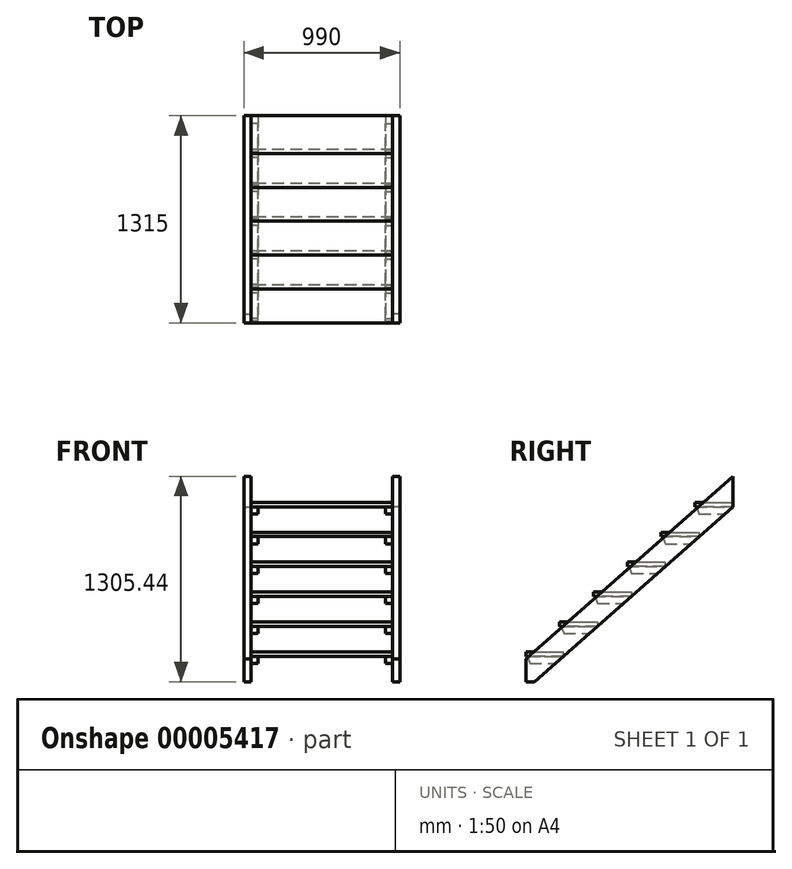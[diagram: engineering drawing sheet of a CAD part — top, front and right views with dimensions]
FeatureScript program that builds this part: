
annotation { "Feature Type Name" : "Feature", "Feature Type Description" : "" }
export const myFeature = defineFeature(function(context is Context, id is Id, definition is map)
    precondition{}
    {
        {
            var Q0;
            Q0=qCreatedBy(makeId("Right.planeOp"),FACE);
            var sketch = newSketch(context, id + "F0", { "sketchPlane" : qUnion([Q0])});
            skLineSegment(sketch, "E0.bottom", {"start": v(0, 0) * mm, "end": v(240, 0) * mm});
            skLineSegment(sketch, "E0.top", {"start": v(0, 28) * mm, "end": v(240, 28) * mm});
            skLineSegment(sketch, "E0.left", {"start": v(0, 0) * mm, "end": v(0, 28) * mm});
            skLineSegment(sketch, "E0.right", {"start": v(240, 0) * mm, "end": v(240, 28) * mm});
            skLineSegment(sketch, "E1.bottom", {"start": v(215, 218) * mm, "end": v(455, 218) * mm});
            skLineSegment(sketch, "E1.top", {"start": v(215, 190) * mm, "end": v(455, 190) * mm});
            skLineSegment(sketch, "E1.left", {"start": v(215, 218) * mm, "end": v(215, 190) * mm});
            skLineSegment(sketch, "E1.right", {"start": v(455, 218) * mm, "end": v(455, 190) * mm});
            skLineSegment(sketch, "E2.bottom", {"start": v(430, 408) * mm, "end": v(670, 408) * mm});
            skLineSegment(sketch, "E2.top", {"start": v(430, 380) * mm, "end": v(670, 380) * mm});
            skLineSegment(sketch, "E2.left", {"start": v(430, 408) * mm, "end": v(430, 380) * mm});
            skLineSegment(sketch, "E2.right", {"start": v(670, 408) * mm, "end": v(670, 380) * mm});
            skLineSegment(sketch, "E3.bottom", {"start": v(645, 598) * mm, "end": v(885, 598) * mm});
            skLineSegment(sketch, "E3.top", {"start": v(645, 570) * mm, "end": v(885, 570) * mm});
            skLineSegment(sketch, "E3.left", {"start": v(645, 598) * mm, "end": v(645, 570) * mm});
            skLineSegment(sketch, "E3.right", {"start": v(885, 598) * mm, "end": v(885, 570) * mm});
            skLineSegment(sketch, "E4.bottom", {"start": v(860, 788) * mm, "end": v(1100, 788) * mm});
            skLineSegment(sketch, "E4.top", {"start": v(860, 760) * mm, "end": v(1100, 760) * mm});
            skLineSegment(sketch, "E4.left", {"start": v(860, 788) * mm, "end": v(860, 760) * mm});
            skLineSegment(sketch, "E4.right", {"start": v(1100, 788) * mm, "end": v(1100, 760) * mm});
            skLineSegment(sketch, "E5.bottom", {"start": v(1075, 978) * mm, "end": v(1315, 978) * mm});
            skLineSegment(sketch, "E5.top", {"start": v(1075, 950) * mm, "end": v(1315, 950) * mm});
            skLineSegment(sketch, "E5.left", {"start": v(1075, 978) * mm, "end": v(1075, 950) * mm});
            skLineSegment(sketch, "E5.right", {"start": v(1315, 978) * mm, "end": v(1315, 950) * mm});
            skSolve(sketch);
        }
        {
            var Q0;
            Q0=makeQuery(id+"F0.imprint","IMPRINT",FACE,{"disambiguationData":[TD([[makeQuery(id+"F0.imprint","IMPRINT",EDGE,{"derivedFrom":sQuery(id+"F0.wireOp",EDGE,"E0.bottom")}),1.0]])]});
            var Q1;
            Q1=makeQuery(id+"F0.imprint","IMPRINT",FACE,{"disambiguationData":[TD([[makeQuery(id+"F0.imprint","IMPRINT",EDGE,{"derivedFrom":sQuery(id+"F0.wireOp",EDGE,"E1.bottom")}),-1.0]])]});
            var Q2;
            Q2=makeQuery(id+"F0.imprint","IMPRINT",FACE,{"disambiguationData":[TD([[makeQuery(id+"F0.imprint","IMPRINT",EDGE,{"derivedFrom":sQuery(id+"F0.wireOp",EDGE,"E4.bottom")}),-1.0]])]});
            var Q3;
            Q3=makeQuery(id+"F0.imprint","IMPRINT",FACE,{"disambiguationData":[TD([[makeQuery(id+"F0.imprint","IMPRINT",EDGE,{"derivedFrom":sQuery(id+"F0.wireOp",EDGE,"E3.bottom")}),-1.0]])]});
            var Q4;
            Q4=makeQuery(id+"F0.imprint","IMPRINT",FACE,{"disambiguationData":[TD([[makeQuery(id+"F0.imprint","IMPRINT",EDGE,{"derivedFrom":sQuery(id+"F0.wireOp",EDGE,"E5.bottom")}),-1.0]])]});
            var Q5;
            Q5=makeQuery(id+"F0.imprint","IMPRINT",FACE,{"disambiguationData":[TD([[makeQuery(id+"F0.imprint","IMPRINT",EDGE,{"derivedFrom":sQuery(id+"F0.wireOp",EDGE,"E2.bottom")}),-1.0]])]});
            var Q6;
            Q6=makeQuery(id+"F0.imprint","IMPRINT",FACE,{"disambiguationData":[TD([[makeQuery(id+"F0.imprint","IMPRINT",EDGE,{"derivedFrom":sQuery(id+"F0.wireOp",EDGE,"670252bf-9cfb-4d57-b23d-327e6f0d2165.bottom")}),-1.0]])]});
            var Q7;
            Q7=makeQuery(id+"F0.imprint","IMPRINT",FACE,{"disambiguationData":[TD([[makeQuery(id+"F0.imprint","IMPRINT",EDGE,{"derivedFrom":sQuery(id+"F0.wireOp",EDGE,"97e81333-a598-4cda-a3b6-67043b5d0b65.bottom")}),-1.0]])]});
            extrude(context, id + "F1", {"entities" : qUnion([Q0, Q1, Q2, Q3, Q4, Q5, Q6, Q7]), "depth" : 900 * mm});
        }
        {
            var Q0;
            Q0=makeQuery(id+"F1.opExtrude","CAP_FACE",FACE,{"disambiguationData":[OSD([sQuery(id+"F0.wireOp",EDGE,"E0.bottom"),sQuery(id+"F0.wireOp",EDGE,"E0.top"),sQuery(id+"F0.wireOp",EDGE,"E0.left"),sQuery(id+"F0.wireOp",EDGE,"E0.right")])],"isStart":false});
            var sketch = newSketch(context, id + "F2", { "sketchPlane" : qUnion([Q0])});
            skLineSegment(sketch, "E6", {"start": v(55.73, -162) * mm, "end": v(0, -162) * mm});
            skLineSegment(sketch, "E7", {"start": v(0, -17.77) * mm, "end": v(1127.65, 978) * mm});
            skLineSegment(sketch, "E8", {"start": v(1127.65, 978) * mm, "end": v(1315, 978) * mm});
            skLineSegment(sketch, "E9", {"start": v(1315, 978) * mm, "end": v(1315, 950) * mm});
            skLineSegment(sketch, "E10", {"start": v(1315, 950) * mm, "end": v(55.73, -162) * mm});
            skLineSegment(sketch, "E11", {"start": v(1315, 978) * mm, "end": v(1315, 1143.44) * mm});
            skLineSegment(sketch, "E12", {"start": v(1127.65, 978) * mm, "end": v(1315, 1143.44) * mm});
            skLineSegment(sketch, "E13", {"start": v(0, -17.77) * mm, "end": v(0, -162) * mm});
            skSolve(sketch);
        }
        {
            var Q0;
            Q0 = qSketchRegion(id + "F2", true);
            extrude(context, id + "F3", {"entities" : qUnion([Q0]), "depth" : 45 * mm});
        }
        {
            var Q0;
            Q0=makeQuery(id+"F3.opExtrude","CAP_FACE",FACE,{"disambiguationData":[OSD([sQuery(id+"F2.wireOp",EDGE,"E6"),sQuery(id+"F2.wireOp",EDGE,"708b9f7f-88d3-4525-9253-f1f07b30f08b"),sQuery(id+"F2.wireOp",EDGE,"E7"),sQuery(id+"F2.wireOp",EDGE,"E8"),sQuery(id+"F2.wireOp",EDGE,"E9"),sQuery(id+"F2.wireOp",EDGE,"E10")])],"isStart":true});
            var sketch = newSketch(context, id + "F4", { "sketchPlane" : qUnion([Q0])});
            skLineSegment(sketch, "E14", {"start": v(-1315, 950) * mm, "end": v(-1085, 950) * mm});
            skLineSegment(sketch, "E15", {"start": v(-1085, 950) * mm, "end": v(-1101.38, 905) * mm});
            skLineSegment(sketch, "E16", {"start": v(-1101.38, 905) * mm, "end": v(-1264.04, 905) * mm});
            skLineSegment(sketch, "E17", {"start": v(-1264.04, 905) * mm, "end": v(-1315, 950) * mm});
            skLineSegment(sketch, "E18", {"start": v(-1099.84, 760) * mm, "end": v(-870, 760) * mm});
            skLineSegment(sketch, "E19", {"start": v(-870, 760) * mm, "end": v(-886.38, 715) * mm});
            skLineSegment(sketch, "E20", {"start": v(-886.38, 715) * mm, "end": v(-1048.88, 715) * mm});
            skLineSegment(sketch, "E21", {"start": v(-1048.88, 715) * mm, "end": v(-1099.84, 760) * mm});
            skLineSegment(sketch, "E22", {"start": v(-884.68, 570) * mm, "end": v(-655, 570) * mm});
            skLineSegment(sketch, "E23", {"start": v(-655, 570) * mm, "end": v(-671.38, 525) * mm});
            skLineSegment(sketch, "E24", {"start": v(-671.38, 525) * mm, "end": v(-833.72, 525) * mm});
            skLineSegment(sketch, "E25", {"start": v(-833.72, 525) * mm, "end": v(-884.68, 570) * mm});
            skLineSegment(sketch, "E26", {"start": v(-669.51, 380) * mm, "end": v(-440, 380) * mm});
            skLineSegment(sketch, "E27", {"start": v(-440, 380) * mm, "end": v(-456.38, 335) * mm});
            skLineSegment(sketch, "E28", {"start": v(-456.38, 335) * mm, "end": v(-618.55, 335) * mm});
            skLineSegment(sketch, "E29", {"start": v(-618.55, 335) * mm, "end": v(-669.51, 380) * mm});
            skLineSegment(sketch, "E30", {"start": v(-454.35, 190) * mm, "end": v(-225, 190) * mm});
            skLineSegment(sketch, "E31", {"start": v(-225, 190) * mm, "end": v(-241.38, 145) * mm});
            skLineSegment(sketch, "E32", {"start": v(-241.38, 145) * mm, "end": v(-403.4, 145) * mm});
            skLineSegment(sketch, "E33", {"start": v(-403.4, 145) * mm, "end": v(-454.35, 190) * mm});
            skLineSegment(sketch, "E34", {"start": v(-239.19, 0) * mm, "end": v(-10, 0) * mm});
            skLineSegment(sketch, "E35", {"start": v(-10, 0) * mm, "end": v(-26.38, -45) * mm});
            skLineSegment(sketch, "E36", {"start": v(-26.38, -45) * mm, "end": v(-188.23, -45) * mm});
            skLineSegment(sketch, "E37", {"start": v(-188.23, -45) * mm, "end": v(-239.19, 0) * mm});
            skSolve(sketch);
        }
        {
            var Q0;
            Q0 = qSketchRegion(id + "F4", true);
            extrude(context, id + "F5", {"entities" : qUnion([Q0]), "depth" : 45 * mm});
        }
        {
            var Q0;
            Q0=makeQuery(id+"F3.opExtrude","CAP_FACE",FACE,{"disambiguationData":[OSD([sQuery(id+"F2.wireOp",EDGE,"E6"),sQuery(id+"F2.wireOp",EDGE,"708b9f7f-88d3-4525-9253-f1f07b30f08b"),sQuery(id+"F2.wireOp",EDGE,"E7"),sQuery(id+"F2.wireOp",EDGE,"E8"),sQuery(id+"F2.wireOp",EDGE,"E9"),sQuery(id+"F2.wireOp",EDGE,"E10")])],"isStart":true});
            cPlane(context, id + "F6", {"entities" : qUnion([Q0]), "cplaneType" : CPlaneType.OFFSET, "offset" : 450 * mm, "width" : 150 * mm, "height" : 150 * mm});
        }
        {
            var Q0;
            Q0=makeQuery(id+"F3.opExtrude","SWEPT_BODY",BODY,{"disambiguationData":[OSD([sQuery(id+"F2.wireOp",EDGE,"E6"),sQuery(id+"F2.wireOp",EDGE,"708b9f7f-88d3-4525-9253-f1f07b30f08b"),sQuery(id+"F2.wireOp",EDGE,"E7"),sQuery(id+"F2.wireOp",EDGE,"E8"),sQuery(id+"F2.wireOp",EDGE,"E9"),sQuery(id+"F2.wireOp",EDGE,"E10")])]});
            var Q1;
            Q1=makeQuery(id+"F5.opExtrude","SWEPT_BODY",BODY,{"disambiguationData":[OSD([sQuery(id+"F4.wireOp",EDGE,"594b4c31-2df9-4f52-b610-abc5414cfb62"),sQuery(id+"F4.wireOp",EDGE,"86ebf6da-c51f-4833-ad60-2c0892496baf"),sQuery(id+"F4.wireOp",EDGE,"252fbf8b-e5cf-435e-b5a5-f1e215c7401b"),sQuery(id+"F4.wireOp",EDGE,"c9fd7e47-7c23-4352-acdb-89b1828a9464")])]});
            var Q2;
            Q2=makeQuery(id+"F5.opExtrude","SWEPT_BODY",BODY,{"disambiguationData":[OSD([sQuery(id+"F4.wireOp",EDGE,"6c800648-40d1-4697-8e4a-4d96ba12bec2"),sQuery(id+"F4.wireOp",EDGE,"f4c406b4-7465-49e5-89fc-65988e7ad4f1"),sQuery(id+"F4.wireOp",EDGE,"f1dea9f2-ef0d-47aa-8200-977d984ce0e3"),sQuery(id+"F4.wireOp",EDGE,"45f3bbd9-ee45-4249-b0af-515ac59857dc")])]});
            var Q3;
            Q3=makeQuery(id+"F5.opExtrude","SWEPT_BODY",BODY,{"disambiguationData":[OSD([sQuery(id+"F4.wireOp",EDGE,"E14"),sQuery(id+"F4.wireOp",EDGE,"E15"),sQuery(id+"F4.wireOp",EDGE,"E16"),sQuery(id+"F4.wireOp",EDGE,"E17")])]});
            var Q4;
            Q4=makeQuery(id+"F5.opExtrude","SWEPT_BODY",BODY,{"disambiguationData":[OSD([sQuery(id+"F4.wireOp",EDGE,"E18"),sQuery(id+"F4.wireOp",EDGE,"E19"),sQuery(id+"F4.wireOp",EDGE,"E20"),sQuery(id+"F4.wireOp",EDGE,"E21")])]});
            var Q5;
            Q5=makeQuery(id+"F5.opExtrude","SWEPT_BODY",BODY,{"disambiguationData":[OSD([sQuery(id+"F4.wireOp",EDGE,"E22"),sQuery(id+"F4.wireOp",EDGE,"E23"),sQuery(id+"F4.wireOp",EDGE,"E24"),sQuery(id+"F4.wireOp",EDGE,"E25")])]});
            var Q6;
            Q6=makeQuery(id+"F5.opExtrude","SWEPT_BODY",BODY,{"disambiguationData":[OSD([sQuery(id+"F4.wireOp",EDGE,"E26"),sQuery(id+"F4.wireOp",EDGE,"E27"),sQuery(id+"F4.wireOp",EDGE,"E28"),sQuery(id+"F4.wireOp",EDGE,"E29")])]});
            var Q7;
            Q7=makeQuery(id+"F5.opExtrude","SWEPT_BODY",BODY,{"disambiguationData":[OSD([sQuery(id+"F4.wireOp",EDGE,"E30"),sQuery(id+"F4.wireOp",EDGE,"E31"),sQuery(id+"F4.wireOp",EDGE,"E32"),sQuery(id+"F4.wireOp",EDGE,"E33")])]});
            var Q8;
            Q8=makeQuery(id+"F5.opExtrude","SWEPT_BODY",BODY,{"disambiguationData":[OSD([sQuery(id+"F4.wireOp",EDGE,"E34"),sQuery(id+"F4.wireOp",EDGE,"E35"),sQuery(id+"F4.wireOp",EDGE,"E36"),sQuery(id+"F4.wireOp",EDGE,"E37")])]});
            var Q9;
            Q9=qCreatedBy(id+"F6.planeOp",FACE);
            mirror(context, id + "F7", {"entities" : qUnion([Q0, Q1, Q2, Q3, Q4, Q5, Q6, Q7, Q8]), "mirrorPlane" : qUnion([Q9])});
        }
    });
